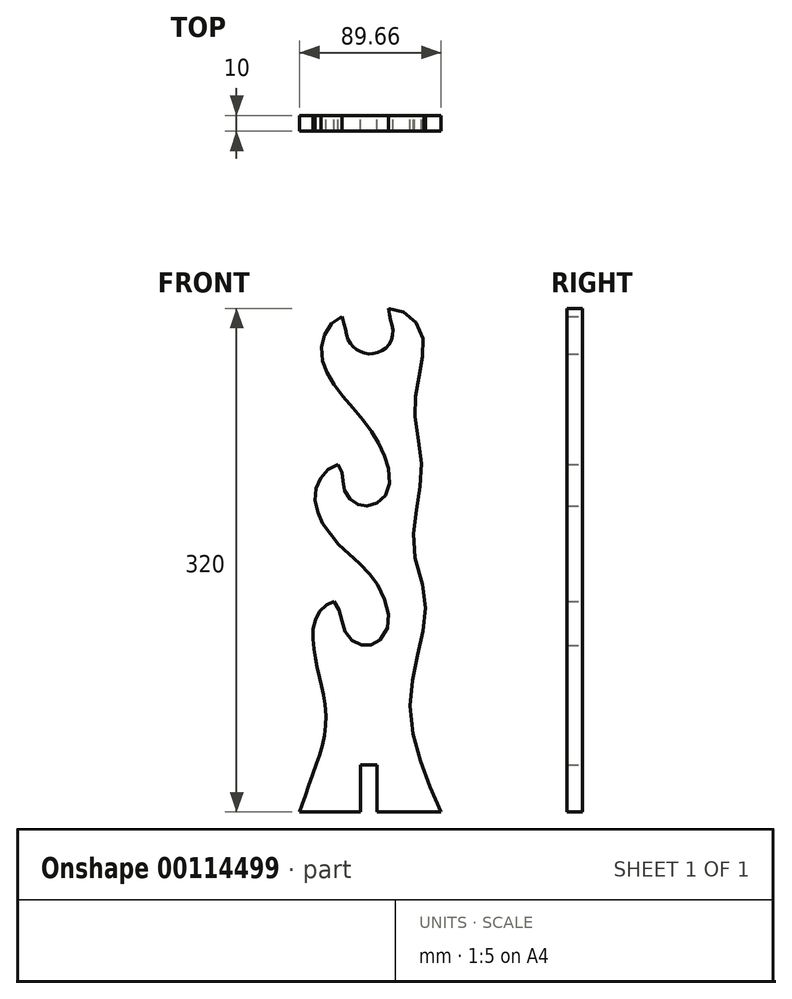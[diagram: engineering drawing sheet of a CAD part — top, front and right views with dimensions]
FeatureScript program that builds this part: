
annotation { "Feature Type Name" : "Feature", "Feature Type Description" : "" }
export const myFeature = defineFeature(function(context is Context, id is Id, definition is map)
    precondition{}
    {
        {
            var Q0;
            Q0=qCreatedBy(makeId("Front.planeOp"),FACE);
            var sketch = newSketch(context, id + "F0", { "sketchPlane" : qUnion([Q0])});
            skLineSegment(sketch, "E0.bottom", {"start": v(-5.25, 0) * mm, "end": v(5.25, 0) * mm});
            skLineSegment(sketch, "E0.top", {"start": v(-5.25, 30) * mm, "end": v(5.25, 30) * mm});
            skLineSegment(sketch, "E0.left", {"start": v(-5.25, 0) * mm, "end": v(-5.25, 30) * mm});
            skLineSegment(sketch, "E0.right", {"start": v(5.25, 0) * mm, "end": v(5.25, 30) * mm});
            skLineSegment(sketch, "E1", {"start": v(0, 0) * mm, "end": v(0, 320) * mm, "construction": true});
            skLineSegment(sketch, "E2", {"start": v(-88.82, 320) * mm, "end": v(88.82, 320) * mm, "construction": true});
            skLineSegment(sketch, "E3", {"start": v(5.25, 0) * mm, "end": v(45.7, 0) * mm});
            skLineSegment(sketch, "E4", {"start": v(-5.25, 0) * mm, "end": v(-43.95, 0) * mm});
            skFitSpline(sketch, "E5", {"points": [v(45.7, 0) * mm, v(36.67, 21.72) * mm, v(29.27, 44.34) * mm, v(25.98, 68.19) * mm, v(28.44, 88.34) * mm, v(32.97, 108.07) * mm, v(35.85, 125.75) * mm, v(34.61, 142.2) * mm, v(28.86, 164) * mm, v(28.86, 182.09) * mm, v(31.32, 198.95) * mm, v(33.38, 216.22) * mm, v(32.14, 231.43) * mm, v(29.27, 249.93) * mm, v(29.27, 262.68) * mm, v(31.32, 274.6) * mm, v(33.94, 288.02) * mm, v(34.72, 298.6) * mm, v(32, 307.9) * mm, v(25.99, 314.8) * mm, v(19.87, 318.58) * mm, v(12.4, 320) * mm], "startDerivative": vector(-159.21, 370.38) * mm, "endDerivative": vector(-234.27, 26.53) * mm});
            skFitSpline(sketch, "E6", {"points": [v(12.4, 320) * mm, v(13.8, 311.92) * mm, v(15.2, 305.82) * mm, v(14.23, 299.72) * mm, v(11.5, 295.47) * mm, v(6.71, 292.2) * mm, v(1.81, 291.11) * mm, v(-2.54, 291.44) * mm, v(-6.9, 293.18) * mm, v(-10.39, 296.01) * mm, v(-13, 299.72) * mm, v(-14.85, 306.25) * mm, v(-16.16, 311.59) * mm, v(-17.14, 314.75) * mm], "startDerivative": vector(12.07, -88.37) * mm, "endDerivative": vector(-16.1, 49.1) * mm});
            skFitSpline(sketch, "E7", {"points": [v(-17.14, 314.75) * mm, v(-22.46, 311.65) * mm, v(-26.73, 306.22) * mm, v(-29.21, 300.22) * mm, v(-30.25, 294.92) * mm, v(-29.73, 287.3) * mm, v(-27.88, 281.59) * mm, v(-24.71, 275.65) * mm, v(-20.61, 269.01) * mm, v(-14.79, 262.03) * mm, v(-9.3, 255.45) * mm, v(-3.42, 248.3) * mm, v(1.2, 242.3) * mm, v(4.54, 236.93) * mm, v(8.58, 229.26) * mm, v(10.89, 223.43) * mm, v(12.62, 216.45) * mm, v(12.85, 207.74) * mm, v(11, 202.09) * mm, v(7.54, 197.88) * mm, v(3.96, 195.57) * mm, v(-0.77, 194.36) * mm, v(-3.08, 194.41) * mm, v(-6.83, 195.28) * mm, v(-9.25, 196.6) * mm, v(-12.77, 199.5) * mm, v(-14.73, 202.43) * mm, v(-16.06, 206.13) * mm, v(-16.4, 209.76) * mm, v(-16.81, 212.47) * mm, v(-17.14, 215.41) * mm, v(-18.25, 217.9) * mm, v(-19.75, 220.9) * mm], "startDerivative": vector(-167.83, -79.5) * mm, "endDerivative": vector(-61.54, 126.78) * mm});
            skFitSpline(sketch, "E8", {"points": [v(-19.75, 220.9) * mm, v(-22.46, 219.86) * mm, v(-26.56, 217.32) * mm, v(-29.44, 214.09) * mm, v(-31.4, 211.2) * mm, v(-33.13, 207.63) * mm, v(-34, 204.51) * mm, v(-34.34, 200.18) * mm, v(-33.71, 194.59) * mm, v(-32.56, 190.66) * mm, v(-31.06, 186.74) * mm, v(-29.1, 182.7) * mm, v(-26.27, 178.84) * mm, v(-22.63, 174) * mm, v(-19.75, 170.47) * mm, v(-15.65, 166.66) * mm, v(-10.63, 162.05) * mm, v(-6.2, 158.12) * mm, v(-1.7, 153.74) * mm, v(1.6, 149.64) * mm, v(4.71, 145.6) * mm, v(8.7, 137.82) * mm, v(11.17, 131.59) * mm, v(12.62, 124.2) * mm, v(12.33, 118.9) * mm, v(10.14, 112.9) * mm, v(6.62, 109.09) * mm, v(2.8, 106.72) * mm, v(1.02, 106.26) * mm, v(-1.29, 105.74) * mm, v(-3.88, 106.09) * mm, v(-7.58, 107.07) * mm, v(-10.23, 108.62) * mm, v(-13.11, 111.28) * mm, v(-15.2, 114.4) * mm, v(-16.29, 117.45) * mm, v(-17.21, 121.66) * mm, v(-18.25, 125.59) * mm, v(-19.25, 129.22) * mm, v(-20.96, 132.1) * mm, v(-22.23, 133.78) * mm], "startDerivative": vector(-126.58, -42.45) * mm, "endDerivative": vector(-70.4, 90.41) * mm});
            skFitSpline(sketch, "E9", {"points": [v(-22.23, 133.78) * mm, v(-25.63, 132.45) * mm, v(-28.98, 130.14) * mm, v(-32.33, 126.05) * mm, v(-34.17, 121.32) * mm, v(-35.44, 116.93) * mm, v(-35.61, 111.57) * mm, v(-35.27, 106.2) * mm, v(-34.75, 101.24) * mm, v(-33.83, 96.62) * mm, v(-32.96, 92.35) * mm, v(-31.63, 86.53) * mm, v(-30.65, 82.14) * mm, v(-29.5, 77.53) * mm, v(-28.7, 73.32) * mm, v(-27.83, 68) * mm, v(-27.3, 61.2) * mm, v(-27.42, 56.47) * mm, v(-27.83, 50.53) * mm, v(-28.75, 45.91) * mm, v(-30.13, 40.14) * mm, v(-31.92, 34.55) * mm, v(-33.08, 31.43) * mm, v(-35.56, 24.16) * mm, v(-38.27, 16.95) * mm, v(-40.06, 11.53) * mm, v(-41.79, 6.68) * mm, v(-43.46, 2.18) * mm, v(-43.95, 0) * mm], "startDerivative": vector(-113.74, -38.5) * mm, "endDerivative": vector(-14.42, -83.7) * mm});
            skSolve(sketch);
        }
        {
            var Q0;
            Q0=makeQuery(id+"F0.imprint","IMPRINT",FACE,{"disambiguationData":[TD([[makeQuery(id+"F0.imprint","IMPRINT",EDGE,{"derivedFrom":sQuery(id+"F0.wireOp",EDGE,"E0.top")}),1.0]])]});
            extrude(context, id + "F1", {"entities" : qUnion([Q0]), "endBound" : BoundingType.SYMMETRIC, "depth" : 10 * mm});
        }
    });
